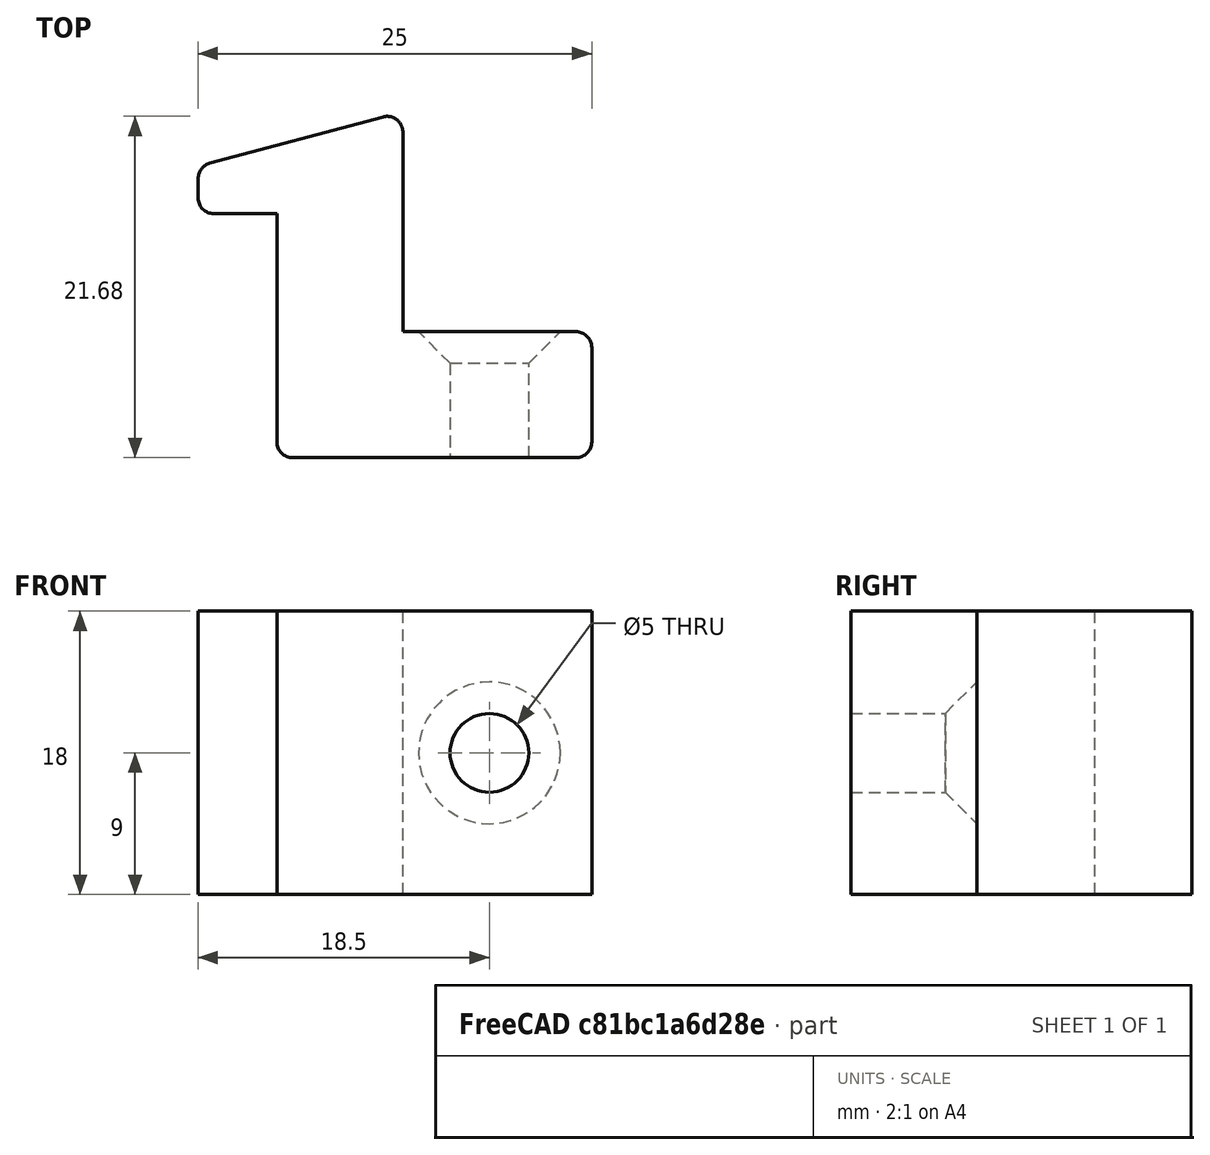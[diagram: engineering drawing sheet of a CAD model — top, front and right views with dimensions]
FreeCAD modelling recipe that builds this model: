
FCSTD DOCUMENT  (FreeCAD 0.19R)
Label: AAChargerClip
License: All rights reserved
LicenseURL: http://en.wikipedia.org/wiki/All_rights_reserved
objects: Sketcher::SketchObject×2, PartDesign::Pad×1, PartDesign::Pocket×1, PartDesign::Chamfer×1, PartDesign::Fillet×1, PartDesign::Body×1, Mesh::Feature×1
note: 11 computed .brp shape members not serialized (recipe doc carries the construction recipe); baked Part::Feature solids carry a one-line shape summary decoded from their .brp

FEATURE [Sketcher::SketchObject] Sketch
  FullyConstrained = true
  MapMode = 5
  Support = -> [XY_Plane]
  sketch-geometry (8):
    g0: LineSegment StartX=0 StartY=-8 StartZ=0 EndX=0 EndY=7.5 EndZ=0
    g1: LineSegment StartX=0 StartY=7.5 StartZ=0 EndX=-5 EndY=7.5 EndZ=0
    g2: LineSegment StartX=-5 StartY=7.5 StartZ=0 EndX=-5 EndY=10.5 EndZ=0
    g3: LineSegment StartX=-5 StartY=10.5 StartZ=0 EndX=8 EndY=13.9833 EndZ=0
    g4: LineSegment StartX=8 StartY=13.9833 StartZ=0 EndX=8 EndY=0 EndZ=0
    g5: LineSegment StartX=8 StartY=0 StartZ=0 EndX=20 EndY=0 EndZ=0
    g6: LineSegment StartX=20 StartY=0 StartZ=0 EndX=20 EndY=-8 EndZ=0
    g7: LineSegment StartX=20 StartY=-8 StartZ=0 EndX=0 EndY=-8 EndZ=0
  constraints (24):
    c: PointOnObject(g0,g-2)
    c: PointOnObject(g0,g-2)
    c: Coincident(g0,g1)
    c: Coincident(g1,g2)
    c: Vertical(g2)
    c: Coincident(g2,g3)
    c: Coincident(g3,g4)
    c: PointOnObject(g4,g-1)
    c: Vertical(g4)
    c: Coincident(g4,g5)
    c: PointOnObject(g5,g-1)
    c: Coincident(g5,g6)
    c: Coincident(g6,g7)
    c: Coincident(g7,g0)
    c: Horizontal(g7)
    c: Vertical(g6)
    c: Horizontal(g1)
    c: Distance(g1) = 5
    c: Distance(g2) = 3
    c: Distance(g4,g0) = 8
    c: Distance(g6) = 8
    c: Distance(g7) = 20
    c: Distance(g0) = 15.5
    c: Angle(g3) = 0.261799
FEATURE [PartDesign::Pad] Pad
  Direction = (1,1,1)
  Length = 18
  Length2 = 100
  Profile = -> Sketch
  Type = 0
FEATURE [Sketcher::SketchObject] Sketch001
  FullyConstrained = true
  MapMode = 5
  Placement = pos=(0,0,0) rot=(0,0.707107,0.707107;3.14159rad)
  Support = -> [Pad]
  sketch-geometry (1):
    g0: Circle CenterX=-13.5 CenterY=9 CenterZ=0 NormalX=0 NormalY=0 NormalZ=1 AngleXU=0 Radius=2.5
  constraints (3):
    c: Diameter(g0) = 5
    c: DistanceX(g0) = -13.5
    c: DistanceY(g0) = 9
FEATURE [PartDesign::Pocket] Pocket
  BaseFeature = -> Pad
  Length = 5
  Length2 = 100
  Profile = -> Sketch001
  Type = 1
FEATURE [PartDesign::Chamfer] Chamfer
  Angle = 45
  Base = -> Pocket [Edge23]
  BaseFeature = -> Pocket
  ChamferType = 0
  FlipDirection = false
  Size = 2
  Size2 = 1
  SupportTransform = false
FEATURE [PartDesign::Fillet] Fillet
  Base = -> Chamfer [Edge27,Edge13,Edge6,Edge9,Edge28,Edge29]
  BaseFeature = -> Chamfer
  Radius = 1
  SupportTransform = false
FEATURE [PartDesign::Body] Body
  Group = -> [Sketch,Pad,Sketch001,Pocket,Chamfer,Fillet]
  Origin = -> Origin
  Tip = -> Fillet
FEATURE [Mesh::Feature] Mesh  label="Fillet (Meshed)"
